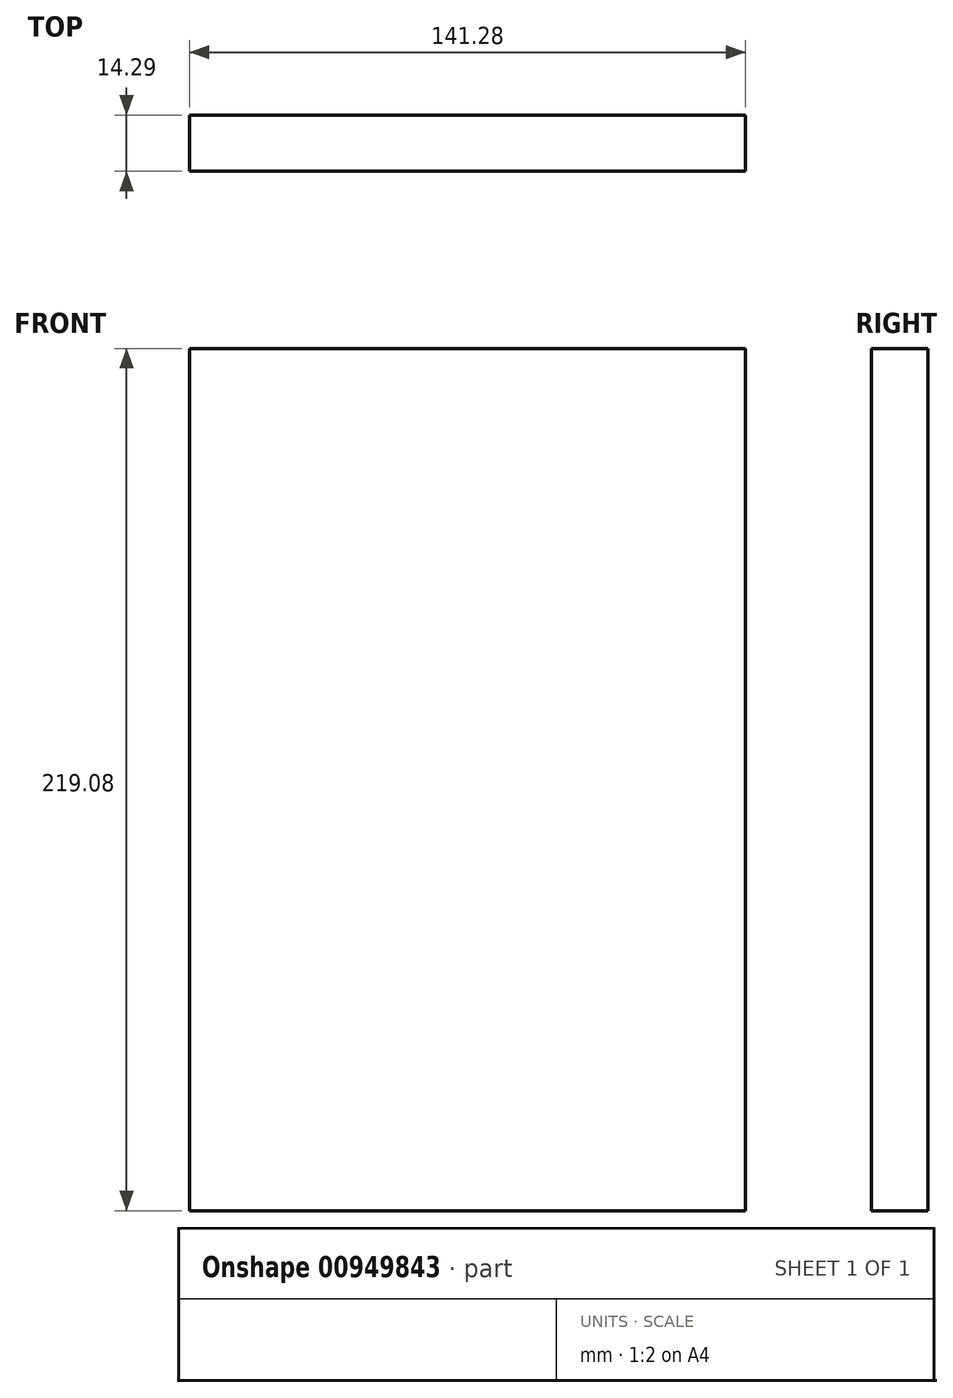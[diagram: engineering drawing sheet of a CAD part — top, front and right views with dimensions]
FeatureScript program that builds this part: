
annotation { "Feature Type Name" : "Feature", "Feature Type Description" : "" }
export const myFeature = defineFeature(function(context is Context, id is Id, definition is map)
    precondition{}
    {
        {
            var Q0;
            Q0=qCreatedBy(makeId("Front.planeOp"),FACE);
            var sketch = newSketch(context, id + "F0", { "sketchPlane" : qUnion([Q0])});
            skLineSegment(sketch, "E0.bottom", {"start": v(-70.64, 109.54) * mm, "end": v(70.64, 109.54) * mm});
            skLineSegment(sketch, "E0.top", {"start": v(-70.64, -109.54) * mm, "end": v(70.64, -109.54) * mm});
            skLineSegment(sketch, "E0.left", {"start": v(-70.64, 109.54) * mm, "end": v(-70.64, -109.54) * mm});
            skLineSegment(sketch, "E0.right", {"start": v(70.64, 109.54) * mm, "end": v(70.64, -109.54) * mm});
            skLineSegment(sketch, "E1", {"start": v(0, 109.54) * mm, "end": v(0, -109.54) * mm, "construction": true});
            skLineSegment(sketch, "E2", {"start": v(-70.64, 0) * mm, "end": v(70.64, 0) * mm, "construction": true});
            skSolve(sketch);
        }
        {
            var Q0;
            Q0=qSketchRegion(id+"F0",true);
            extrude(context, id + "F1", {"entities" : qUnion([Q0]), "depth" : 14.29 * mm, "offsetDistance" : 25.4 * mm});
        }
    });
